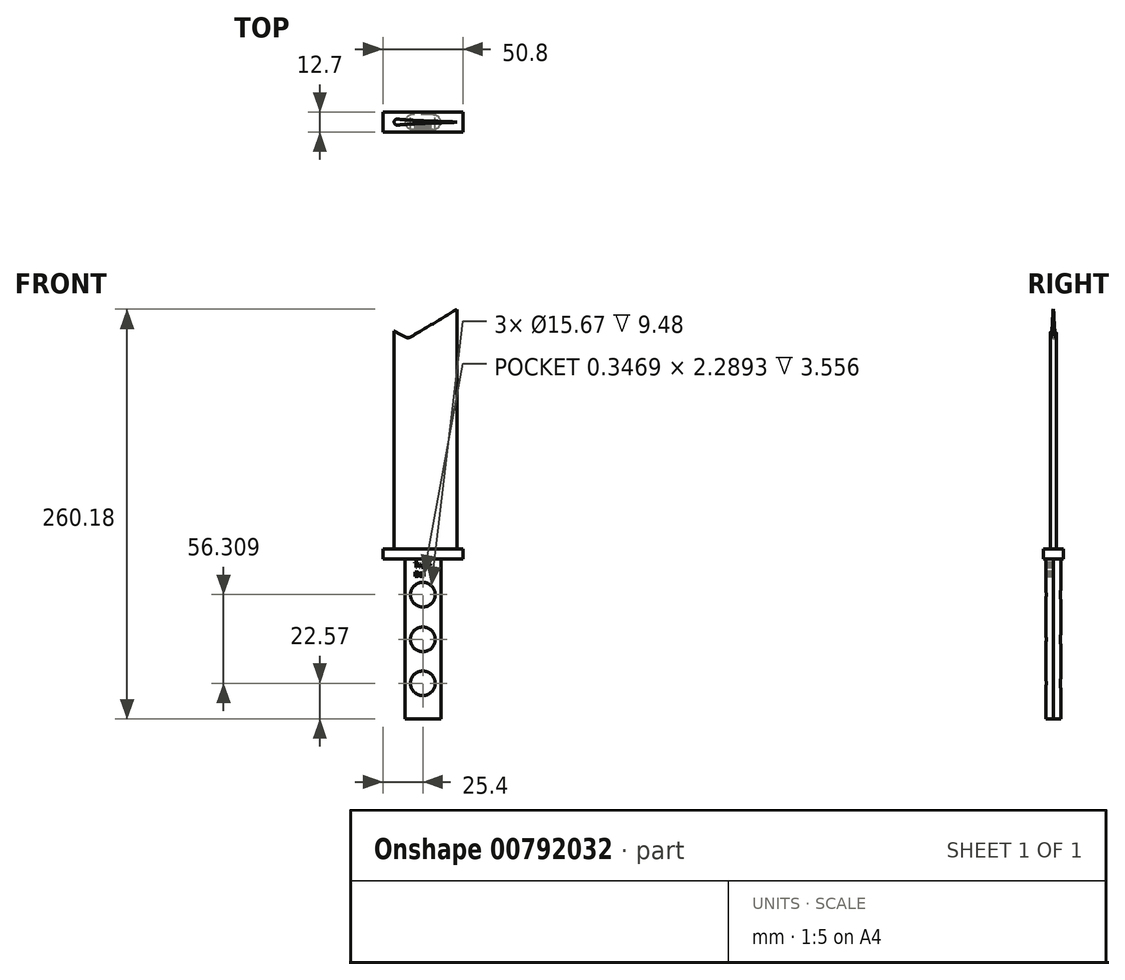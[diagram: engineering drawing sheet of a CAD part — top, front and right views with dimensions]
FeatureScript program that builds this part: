
annotation { "Feature Type Name" : "Feature", "Feature Type Description" : "" }
export const myFeature = defineFeature(function(context is Context, id is Id, definition is map)
    precondition{}
    {
        {
            var Q0;
            Q0=qCreatedBy(makeId("Top.planeOp"),FACE);
            var sketch = newSketch(context, id + "F0", { "sketchPlane" : qUnion([Q0])});
            skLineSegment(sketch, "E0.bottom", {"start": v(25.4, 6.35) * mm, "end": v(-25.4, 6.35) * mm});
            skLineSegment(sketch, "E0.top", {"start": v(25.4, -6.35) * mm, "end": v(-25.4, -6.35) * mm});
            skLineSegment(sketch, "E0.left", {"start": v(25.4, 6.35) * mm, "end": v(25.4, -6.35) * mm});
            skLineSegment(sketch, "E0.right", {"start": v(-25.4, 6.35) * mm, "end": v(-25.4, -6.35) * mm});
            skPoint(sketch, "E0.middle", {"position": v(0, 0) * mm});
            skSolve(sketch);
        }
        {
            var Q0;
            Q0=makeQuery(id+"F0.imprint","IMPRINT",FACE,{"disambiguationData":[TD([[makeQuery(id+"F0.imprint","IMPRINT",EDGE,{"derivedFrom":sQuery(id+"F0.wireOp",EDGE,"E0.bottom")}),1.0]])]});
            extrude(context, id + "F1", {"entities" : qUnion([Q0]), "depth" : 6.35 * mm, "offsetDistance" : 25.4 * mm});
        }
        {
            var Q0;
            Q0=makeQuery(id+"F1.opExtrude","CAP_FACE",FACE,{"disambiguationData":[OSD([sQuery(id+"F0.wireOp",EDGE,"E0.bottom"),sQuery(id+"F0.wireOp",EDGE,"E0.top"),sQuery(id+"F0.wireOp",EDGE,"E0.left"),sQuery(id+"F0.wireOp",EDGE,"E0.right")])],"isStart":true});
            var sketch = newSketch(context, id + "F2", { "sketchPlane" : qUnion([Q0])});
            skLineSegment(sketch, "E1.bottom", {"start": v(11.44, 4.74) * mm, "end": v(-11.44, 4.74) * mm});
            skLineSegment(sketch, "E1.top", {"start": v(11.44, -4.74) * mm, "end": v(-11.44, -4.74) * mm});
            skLineSegment(sketch, "E1.left", {"start": v(11.44, 4.74) * mm, "end": v(11.44, -4.74) * mm});
            skLineSegment(sketch, "E1.right", {"start": v(-11.44, 4.74) * mm, "end": v(-11.44, -4.74) * mm});
            skPoint(sketch, "E1.middle", {"position": v(0, 0) * mm});
            skSolve(sketch);
        }
        {
            var Q0;
            Q0=makeQuery(id+"F2.imprint","IMPRINT",FACE,{"disambiguationData":[TD([[makeQuery(id+"F2.imprint","IMPRINT",EDGE,{"derivedFrom":sQuery(id+"F2.wireOp",EDGE,"E1.bottom")}),1.0]])]});
            extrude(context, id + "F3", {"entities" : qUnion([Q0]), "operationType" : NewBodyOperationType.ADD, "depth" : 101.6 * mm, "offsetDistance" : 25.4 * mm});
        }
        {
            var Q0;
            Q0=makeQuery(id+"F1.opExtrude","CAP_FACE",FACE,{"disambiguationData":[OSD([sQuery(id+"F0.wireOp",EDGE,"E0.bottom"),sQuery(id+"F0.wireOp",EDGE,"E0.top"),sQuery(id+"F0.wireOp",EDGE,"E0.left"),sQuery(id+"F0.wireOp",EDGE,"E0.right")])],"isStart":false});
            var sketch = newSketch(context, id + "F4", { "sketchPlane" : qUnion([Q0])});
            skLineSegment(sketch, "E2", {"start": v(-25.4, 0) * mm, "end": v(25.4, 0) * mm});
            skSolve(sketch);
        }
        {
            var Q0;
            {var subQ0=sQuery(id+"F4.wireOp",EDGE,"E2");Q0=makeQuery(id+"F4.imprint","IMPRINT",FACE,{"disambiguationData":[TD([[makeQuery(id+"F4.imprint","IMPRINT",EDGE,{"derivedFrom":subQ0}),1.0]])]});}
            var sketch = newSketch(context, id + "F5", { "sketchPlane" : qUnion([Q0])});
            skLineSegment(sketch, "E3", {"start": v(-18.25, 2.1) * mm, "end": v(-18.25, 0) * mm});
            skLineSegment(sketch, "E4", {"start": v(-18.25, 0) * mm, "end": v(-18.25, -2.1) * mm});
            skLineSegment(sketch, "E5", {"start": v(-1.88, -0.92) * mm, "end": v(-1.88, 0) * mm});
            skLineSegment(sketch, "E6", {"start": v(-1.88, 0) * mm, "end": v(-1.88, 0.92) * mm});
            skFitSpline(sketch, "E7", {"points": [v(-18.25, -2.1) * mm, v(-1.88, -0.92) * mm, v(21.71, 0) * mm, v(-1.88, 0.92) * mm, v(-18.25, 2.1) * mm], "startDerivative": vector(56.8, 5.64) * mm, "endDerivative": vector(-56.8, 5.64) * mm});
            skSolve(sketch);
        }
        {
            var Q0;
            Q0 = qSketchRegion(id + "F5", true);
            extrude(context, id + "F6", {"entities" : qUnion([Q0]), "operationType" : NewBodyOperationType.ADD, "depth" : 158.75 * mm, "offsetDistance" : 25.4 * mm});
        }
        {
            var Q0;
            Q0=makeQuery(id+"F6.opExtrude","SWEPT_EDGE",EDGE,{"disambiguationData":[OSD([sQuery(id+"F5.wireOp",EDGE,"E4"),sQuery(id+"F5.wireOp",EDGE,"E7")])]});
            fillet(context, id + "F7", {"entities" : qUnion([Q0]), "radius" : 2.07 * mm, "tangentPropagation" : true, "allowEdgeOverflow" : false});
        }
        {
            var Q0;
            Q0=makeQuery(id+"F6.opExtrude","SWEPT_EDGE",EDGE,{"disambiguationData":[OSD([sQuery(id+"F5.wireOp",EDGE,"E3"),sQuery(id+"F5.wireOp",EDGE,"E7")])]});
            fillet(context, id + "F8", {"entities" : qUnion([Q0]), "radius" : 1.87 * mm, "tangentPropagation" : true, "allowEdgeOverflow" : false});
        }
        {
            var Q0;
            Q0=makeQuery(id+"F3.opExtrude","SWEPT_EDGE",EDGE,{"disambiguationData":[OSD([sQuery(id+"F2.wireOp",EDGE,"E1.bottom"),sQuery(id+"F2.wireOp",EDGE,"E1.right")])]});
            var Q1;
            Q1=makeQuery(id+"F3.opExtrude","SWEPT_EDGE",EDGE,{"disambiguationData":[OSD([sQuery(id+"F2.wireOp",EDGE,"E1.top"),sQuery(id+"F2.wireOp",EDGE,"E1.right")])]});
            var Q2;
            Q2=makeQuery(id+"F3.opExtrude","SWEPT_EDGE",EDGE,{"disambiguationData":[OSD([sQuery(id+"F2.wireOp",EDGE,"E1.top"),sQuery(id+"F2.wireOp",EDGE,"E1.left")])]});
            var Q3;
            Q3=makeQuery(id+"F3.opExtrude","SWEPT_EDGE",EDGE,{"disambiguationData":[OSD([sQuery(id+"F2.wireOp",EDGE,"E1.bottom"),sQuery(id+"F2.wireOp",EDGE,"E1.left")])]});
            fillet(context, id + "F9", {"entities" : qUnion([Q0, Q1, Q2, Q3]), "radius" : 5.08 * mm, "tangentPropagation" : true, "allowEdgeOverflow" : false});
        }
        {
            var Q0;
            Q0=makeQuery(id+"F3.opExtrude","SWEPT_FACE",FACE,{"disambiguationData":[OSD([sQuery(id+"F2.wireOp",EDGE,"E1.top")])]});
            var sketch = newSketch(context, id + "F10", { "sketchPlane" : qUnion([Q0])});
            skPoint(sketch, "E8", {"position": v(0, -79.03) * mm});
            skPoint(sketch, "E9", {"position": v(0, -22.72) * mm});
            skPoint(sketch, "E10", {"position": v(0, -51.12) * mm});
            skSolve(sketch);
        }
        {
            var Q0;
            Q0=sQuery(id+"F10.wireOp",VERTEX,"E8");
            var Q1;
            Q1=sQuery(id+"F10.wireOp",VERTEX,"E10");
            var Q2;
            Q2=sQuery(id+"F10.wireOp",VERTEX,"E9");
            var Q3;
            Q3=makeQuery(id+"F1.opExtrude","SWEPT_BODY",BODY,{"disambiguationData":[OSD([sQuery(id+"F0.wireOp",EDGE,"E0.bottom"),sQuery(id+"F0.wireOp",EDGE,"E0.top"),sQuery(id+"F0.wireOp",EDGE,"E0.left"),sQuery(id+"F0.wireOp",EDGE,"E0.right")])]});
            hole(context, id + "F11", {"style" : HoleStyle.SIMPLE, "endStyle" : HoleEndStyle.BLIND, "holeDiameter" : 15.67 * mm, "majorDiameter" : 6.35 * mm, "holeDepth" : 10.16 * mm, "isTappedThrough" : true, "tappedDepth" : 12.7 * mm, "tapClearance" : 3, "locations" : qUnion([Q0, Q1, Q2]), "scope" : qUnion([Q3])});
        }
        {
            var Q0;
            {var subQ0=makeQuery(id+"F1.opExtrude","CAP_FACE",FACE,{"disambiguationData":[OSD([sQuery(id+"F0.wireOp",EDGE,"E0.bottom"),sQuery(id+"F0.wireOp",EDGE,"E0.top"),sQuery(id+"F0.wireOp",EDGE,"E0.left"),sQuery(id+"F0.wireOp",EDGE,"E0.right")])],"isStart":true});var subQ1=sQuery(id+"F2.wireOp",EDGE,"E1.bottom");Q0=makeQuery(id+"F11.hole-2.boolean.opBoolean","SPLIT",FACE,{"disambiguationData":[TD([subQ0])],"derivedFrom":makeQuery(id+"F11.hole-1.boolean.opBoolean","SPLIT",FACE,{"disambiguationData":[TD([subQ0])],"derivedFrom":makeQuery(id+"F11.hole-0.boolean.opBoolean","SPLIT",FACE,{"disambiguationData":[TD([subQ0])],"derivedFrom":makeQuery(id+"F3.opExtrude","SWEPT_FACE",FACE,{"disambiguationData":[OSD([subQ1])]})})})});}
            var sketch = newSketch(context, id + "F12", { "sketchPlane" : qUnion([Q0])});
            skText(sketch, "E11", { "text": "Twee \nBoi                                                                                                              ", "fontName": "OpenSans-Regular.ttf"});
            const initialGuessF12  = {"E11": [-0.00528, -0.00538, 1, 0, 0.00308]};
            skSetInitialGuess(sketch, initialGuessF12);
            skSolve(sketch);
        }
        {
            var Q0;
            Q0 = qSketchRegion(id + "F12", true);
            extrude(context, id + "F13", {"entities" : qUnion([Q0]), "operationType" : NewBodyOperationType.REMOVE, "oppositeDirection" : true, "depth" : 3.56 * mm, "offsetDistance" : 25.4 * mm});
        }
        {
            var Q0;
            Q0=makeQuery(id+"F6.opExtrude","CAP_FACE",FACE,{"disambiguationData":[OSD([sQuery(id+"F5.wireOp",EDGE,"E3"),sQuery(id+"F5.wireOp",EDGE,"E4"),sQuery(id+"F5.wireOp",EDGE,"E7")])],"isStart":false});
            var sketch = newSketch(context, id + "F14", { "sketchPlane" : qUnion([Q0])});
            skPoint(sketch, "E12", {"position": v(-9.76, 0) * mm});
            skSolve(sketch);
        }
        {
            var Q0;
            Q0=sQuery(id+"F14.wireOp",VERTEX,"E12");
            var Q1;
            Q1=makeQuery(id+"F1.opExtrude","SWEPT_BODY",BODY,{"disambiguationData":[OSD([sQuery(id+"F0.wireOp",EDGE,"E0.bottom"),sQuery(id+"F0.wireOp",EDGE,"E0.top"),sQuery(id+"F0.wireOp",EDGE,"E0.left"),sQuery(id+"F0.wireOp",EDGE,"E0.right")])]});
            hole(context, id + "F15", {"style" : HoleStyle.SIMPLE, "endStyle" : HoleEndStyle.BLIND, "holeDiameter" : 63.5 * mm, "majorDiameter" : 6.35 * mm, "holeDepth" : 6.35 * mm, "isTappedThrough" : true, "tappedDepth" : 12.7 * mm, "tapClearance" : 3, "locations" : qUnion([Q0]), "scope" : qUnion([Q1])});
        }
    });
